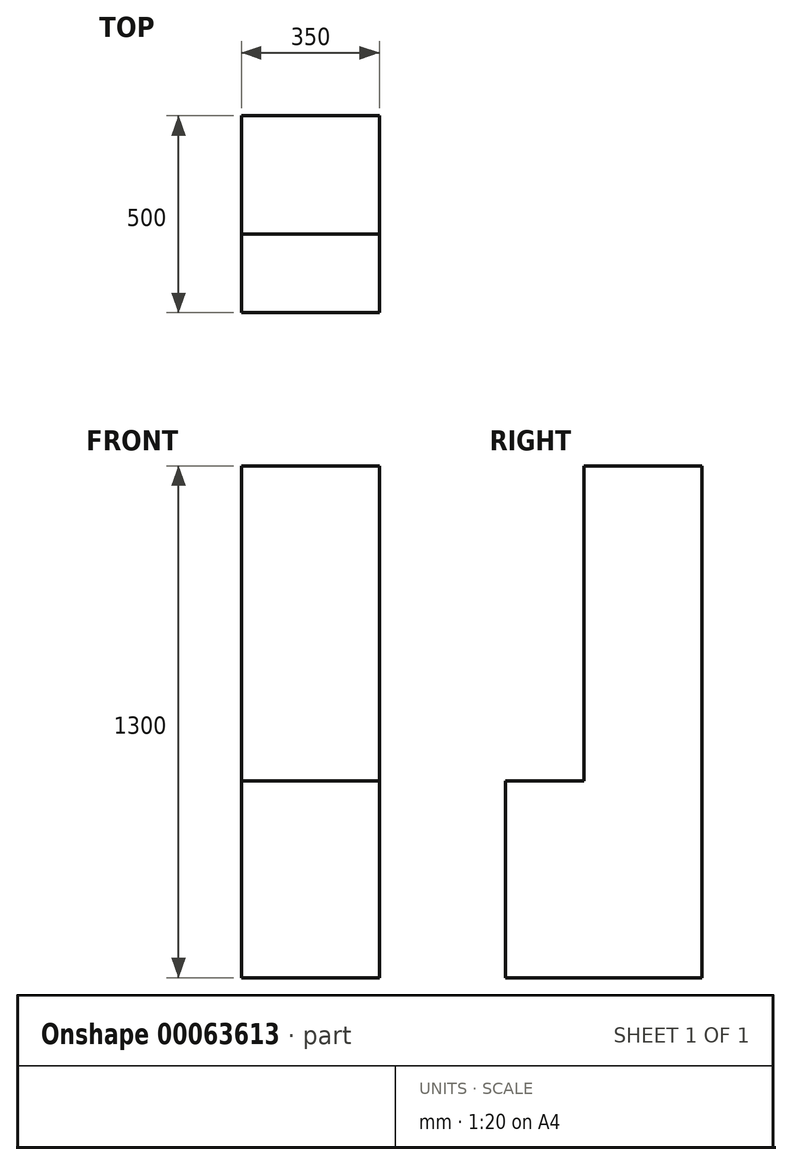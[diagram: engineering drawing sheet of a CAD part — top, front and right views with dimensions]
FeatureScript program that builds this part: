
annotation { "Feature Type Name" : "Feature", "Feature Type Description" : "" }
export const myFeature = defineFeature(function(context is Context, id is Id, definition is map)
    precondition{}
    {
        {
            var Q0;
            Q0=qCreatedBy(makeId("Front.planeOp"),FACE);
            var sketch = newSketch(context, id + "F0", { "sketchPlane" : qUnion([Q0])});
            skLineSegment(sketch, "E0.bottom", {"start": v(0, 0) * mm, "end": v(350, 0) * mm});
            skLineSegment(sketch, "E0.top", {"start": v(0, -500) * mm, "end": v(350, -500) * mm});
            skLineSegment(sketch, "E0.left", {"start": v(0, 0) * mm, "end": v(0, -500) * mm});
            skLineSegment(sketch, "E0.right", {"start": v(350, 0) * mm, "end": v(350, -500) * mm});
            skSolve(sketch);
        }
        {
            var Q0;
            Q0=makeQuery(id+"F0.imprint","IMPRINT",FACE,{"disambiguationData":[TD([[makeQuery(id+"F0.imprint","IMPRINT",EDGE,{"derivedFrom":sQuery(id+"F0.wireOp",EDGE,"E0.bottom")}),-1.0]])]});
            extrude(context, id + "F1", {"entities" : qUnion([Q0]), "depth" : 500 * mm});
        }
        {
            var Q0;
            Q0=makeQuery(id+"F1.opExtrude","SWEPT_FACE",FACE,{"disambiguationData":[OSD([sQuery(id+"F0.wireOp",EDGE,"E0.left")])]});
            var sketch = newSketch(context, id + "F2", { "sketchPlane" : qUnion([Q0])});
            skLineSegment(sketch, "E1.bottom", {"start": v(0, 0) * mm, "end": v(300, 0) * mm});
            skLineSegment(sketch, "E1.top", {"start": v(0, 800) * mm, "end": v(300, 800) * mm});
            skLineSegment(sketch, "E1.left", {"start": v(0, 0) * mm, "end": v(0, 800) * mm});
            skLineSegment(sketch, "E1.right", {"start": v(300, 0) * mm, "end": v(300, 800) * mm});
            skSolve(sketch);
        }
        {
            var Q0;
            Q0=makeQuery(id+"F2.imprint","IMPRINT",FACE,{"disambiguationData":[TD([[makeQuery(id+"F2.imprint","IMPRINT",EDGE,{"derivedFrom":sQuery(id+"F2.wireOp",EDGE,"E1.bottom")}),-1.0]])]});
            extrude(context, id + "F3", {"entities" : qUnion([Q0]), "operationType" : NewBodyOperationType.ADD, "oppositeDirection" : true, "depth" : 350 * mm});
        }
    });
